# Revit family: result
name_source: partatom
category: Generic Models
revit_build: Autodesk Revit 2015 (Build: 20140903_1530(x64)
units: mm (PartAtom-declared; Revit-internal decimal feet)

## types (1)
- Default
    BIMobject category = Toilets
    BIMobject category code = toilets
    BIMobject main category = Sanitary
    BIMobject main category code = sanitary
    Brand url = http://www.duravit.com
    Date of publishing = 5/5/2021
    Design country = Germany
    Edition number = 1
    IFC Classification = Sanitary Terminal
    Installation instructions = https://duravit-public-assets.s3.eu-central-1.amazonaws.com
    Manufacturer name = DURAVIT AG
    Masterformat 2014 Code = 22 41 13.13
    Masterformat 2014 Description = Residential Water Closets
    Material main = Ceramics
    OmniClass Code = 23-31 19 00
    OmniClass Description = Toilets
    Product Guid = 5e5b1a67-ef61-48a4-8f33-f37721e0d8cb
    Product SKU = d-neo-floor-mounted-toilet-for-combination-200209
    Product certification = http://pro.duravit.com
    Product data url = https://bimobject.com
    Product family = Toilets
    Product group = Floorstanding toilet for combination
    Product name = D-Neo Floorstanding toilet for combination White High Gloss 650 mm - 200209
    Product url = https://duravit-public-assets.s3.eu-central-1.amazonaws.com
    QR code = http://bimobject.com
    Technical description = http://pro.duravit.com
    UNSPSC Code = 30181505
    Uniclass 2015 Code = Pr_40_20_93_97
    Uniclass 2015 Name = WC suites
    Uniformat II Code = D2010
    Uniformat II Description = Plumbing Fixtures
    Youtube clip = https://duravit-public-assets.s3.eu-central-1.amazonaws.com

## geometry (parser evidence)
native form markers: Sweep x4
no freeform markers — native parametric forms only
